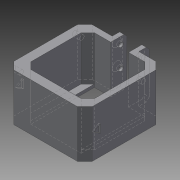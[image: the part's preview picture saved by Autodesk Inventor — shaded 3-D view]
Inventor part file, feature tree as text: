
AUTODESK INVENTOR PART (.ipt)
format: ipt  version: 2015 (Build 190159000, 159)  size: 214,528 bytes
history: native  units: mm
features: sketch x9, extrude x6, chamfer x4, hole x3
ambient origin geometry x8: Origin, YZ Plane, XZ Plane, XY Plane, X Axis, Y Axis, Z Axis, Center Point
bodies: Solid1 (feature_tree)
feature tree (22):
  extrude  "Extrusion1"  Depth=43.0mm
  hole  "Hole1"  [1 undecoded]
  chamfer  "Chamfer1"  Distance=30.0mm
  chamfer  "Chamfer2"  Distance=4.5mm Angle=45.0deg
  extrude  "Extrusion2"  Depth=2.0mm TaperAngle=0.0deg
  chamfer  "Chamfer3"  Distance=5.0mm Angle=45.0deg
  extrude  "Extrusion3"  Depth=7.5mm
  extrude  "Extrusion4"  Depth=10.0mm TaperAngle=0.0deg
  extrude  "Extrusion5"  Depth=1.0mm TaperAngle=0.0deg
  hole  "Hole2"  [1 undecoded]
  chamfer  "Chamfer4"  Distance=3.0mm
  hole  "Hole3"  [1 undecoded]
  extrude  "Extrusion6"  Depth=1.5mm
  sketch  "Sketch1"  dims[d0=43.0mm d1=43.0mm]
  sketch  "Sketch2"  dims[d2=6.0mm d3=4.0mm]
  sketch  "Sketch3"  dims[d4=6.0mm]
  sketch  "Sketch4"  dims[d5=4.0mm d6=30.0mm d7=0.0mm]
  sketch  "Sketch5"  dims[d8=5.0mm]
  sketch  "Sketch6"  dims[d9=41.0mm]
  sketch  "Sketch7"  dims[d10=3.0mm d11=6.0mm d12=4.0mm d13=2.0mm d14=90.0deg d15=5.0mm d16=20.594885mm d17=4.5mm d18=2.0mm d19=45.0deg]
  sketch  "Sketch8"  dims[d20=5.0mm d21=2.0mm d22=45.0deg d23=2.0mm d24=0.0mm d25=5.0mm d26=2.0mm d27=45.0deg]
  sketch  "Sketch9"  dims[d28=15.0mm d29=7.5mm d30=10.0mm d31=0.0mm d32=1.0mm d33=0.0mm d34=3.0mm d35=3.0mm d36=1.5mm d37=1.5mm d38=7.0mm d39=32.0mm d40=0.0mm d41=5.0mm d42=4.0mm d43=4.0mm d44=13.0mm d45=3.0mm d46=6.0mm d47=6.0mm d48=2.0mm d49=90.0deg d50=8.0mm d51=20.594885mm d52=2.0mm d53=2.0mm d54=45.0deg d55=3.0mm d56=6.0mm d57=6.0mm d58=2.0mm d59=90.0deg d60=8.0mm d61=20.594885mm d62=1.0mm d63=0.0mm]
note: 3 required parameter values undecoded (feature->parameter linkage not recoverable at this tier; creation-order binding heuristic only, values carry confidence <= 0.55)
